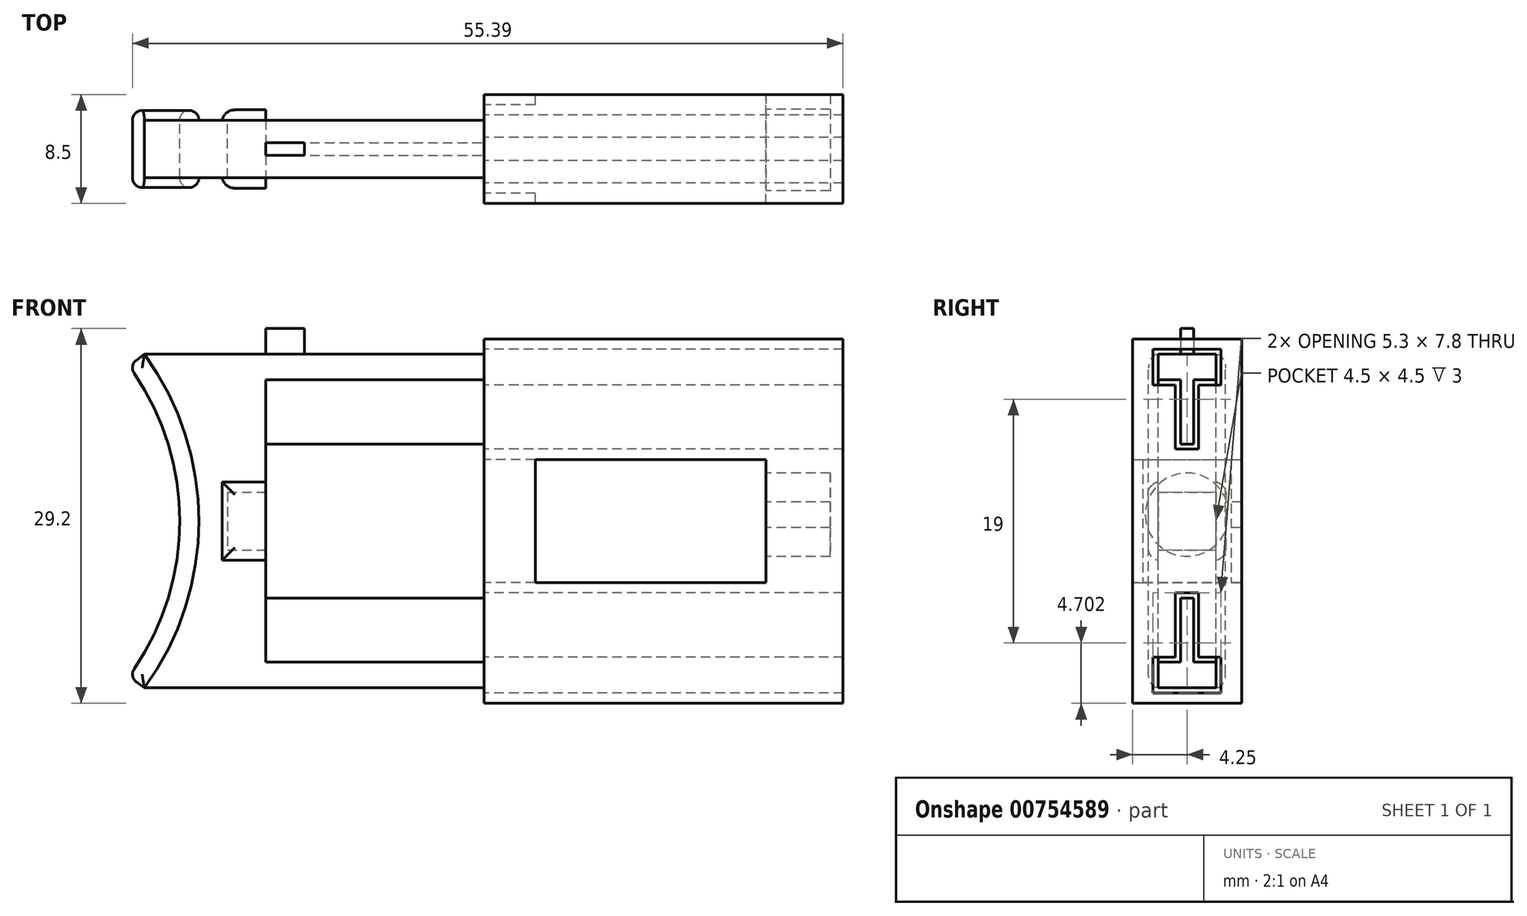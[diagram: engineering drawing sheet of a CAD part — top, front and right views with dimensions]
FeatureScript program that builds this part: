
annotation { "Feature Type Name" : "Feature", "Feature Type Description" : "" }
export const myFeature = defineFeature(function(context is Context, id is Id, definition is map)
    precondition{}
    {
        {
            var Q0;
            Q0=qCreatedBy(makeId("Front.planeOp"),FACE);
            var sketch = newSketch(context, id + "F0", { "sketchPlane" : qUnion([Q0])});
            skLineSegment(sketch, "E0.bottom", {"start": v(-9.54, 1.75) * mm, "end": v(-6.54, 1.75) * mm});
            skLineSegment(sketch, "E0.top", {"start": v(-9.54, -2.75) * mm, "end": v(-6.54, -2.75) * mm});
            skLineSegment(sketch, "E0.left", {"start": v(-9.54, 1.75) * mm, "end": v(-9.54, -2.75) * mm});
            skLineSegment(sketch, "E1.bottom", {"start": v(-16, 12.5) * mm, "end": v(-9.54, 12.5) * mm, "construction": true});
            skLineSegment(sketch, "E1.top", {"start": v(-16, -13.5) * mm, "end": v(-9.54, -13.5) * mm, "construction": true});
            skLineSegment(sketch, "E1.left", {"start": v(-9.54, 12.5) * mm, "end": v(-9.54, -13.5) * mm, "construction": true});
            skLineSegment(sketch, "E1.right", {"start": v(-16, 12.5) * mm, "end": v(-16, -13.5) * mm, "construction": true});
            skPoint(sketch, "E2", {"position": v(-9.54, -0.5) * mm});
            skArc(sketch, "E3", {"start": v(-16, -13.5) * mm, "mid": v(-11.75, -0.5) * mm, "end": v(-16, 12.5) * mm});
            skLineSegment(sketch, "E4", {"start": v(-16, -13.5) * mm, "end": v(10.46, -13.5) * mm});
            skPoint(sketch, "E4.endSnap0", {"position": v(-12.77, -13.5) * mm});
            skLineSegment(sketch, "E5", {"start": v(10.46, -13.5) * mm, "end": v(10.46, -5.75) * mm});
            skLineSegment(sketch, "E6", {"start": v(10.46, -5.75) * mm, "end": v(-6.54, -5.75) * mm});
            skLineSegment(sketch, "E7", {"start": v(-6.54, -5.75) * mm, "end": v(-6.54, -2.75) * mm});
            skLineSegment(sketch, "E8", {"start": v(-6.54, 1.75) * mm, "end": v(-6.54, 4.75) * mm});
            skLineSegment(sketch, "E9", {"start": v(-6.54, 4.75) * mm, "end": v(10.46, 4.75) * mm});
            skLineSegment(sketch, "E10", {"start": v(10.46, 4.75) * mm, "end": v(10.46, 12.5) * mm});
            skLineSegment(sketch, "E11", {"start": v(10.46, 12.5) * mm, "end": v(-16, 12.5) * mm});
            skSolve(sketch);
        }
        {
            var Q0;
            Q0=makeQuery(id+"F0.imprint","IMPRINT",FACE,{"disambiguationData":[TD([[makeQuery(id+"F0.imprint","IMPRINT",EDGE,{"derivedFrom":sQuery(id+"F0.wireOp",EDGE,"E0.bottom")}),1.0]])]});
            extrude(context, id + "F1", {"entities" : qUnion([Q0]), "endBound" : BoundingType.SYMMETRIC, "depth" : 4.5 * mm, "offsetDistance" : 25 * mm});
        }
        {
            var Q0;
            Q0=makeQuery(id+"F1.opExtrude","SWEPT_FACE",FACE,{"disambiguationData":[OSD([sQuery(id+"F0.wireOp",EDGE,"E8")])]});
            var sketch = newSketch(context, id + "F2", { "sketchPlane" : qUnion([Q0])});
            skLineSegment(sketch, "E12.0.0", {"start": v(2.25, -2.75) * mm, "end": v(2.25, 1.75) * mm});
            skLineSegment(sketch, "E12.0.1", {"start": v(2.25, 1.75) * mm, "end": v(-2.25, 1.75) * mm});
            skLineSegment(sketch, "E12.0.2", {"start": v(-2.25, 1.75) * mm, "end": v(-2.25, -2.75) * mm});
            skLineSegment(sketch, "E12.0.3", {"start": v(-2.25, -2.75) * mm, "end": v(2.25, -2.75) * mm});
            skLineSegment(sketch, "E13.0", {"start": v(3.05, -3.55) * mm, "end": v(3.05, 2.55) * mm});
            skLineSegment(sketch, "E13.1", {"start": v(-3.05, -3.55) * mm, "end": v(3.05, -3.55) * mm});
            skLineSegment(sketch, "E13.2", {"start": v(-3.05, 2.55) * mm, "end": v(-3.05, -3.55) * mm});
            skLineSegment(sketch, "E13.3", {"start": v(3.05, 2.55) * mm, "end": v(-3.05, 2.55) * mm});
            skSolve(sketch);
        }
        {
            var Q0;
            Q0 = qSketchRegion(id + "F2", true);
            extrude(context, id + "F3", {"entities" : qUnion([Q0]), "operationType" : NewBodyOperationType.ADD, "oppositeDirection" : true, "depth" : 3.4 * mm, "offsetDistance" : 25 * mm});
        }
        {
            var Q0;
            Q0=qCreatedBy(makeId("Front.planeOp"),FACE);
            var sketch = newSketch(context, id + "F4", { "sketchPlane" : qUnion([Q0])});
            skArc(sketch, "E14.0.0", {"start": v(-16, 12.5) * mm, "mid": v(-11.75, -0.5) * mm, "end": v(-16, -13.5) * mm});
            skArc(sketch, "E14.0.2", {"start": v(-16, -13.5) * mm, "mid": v(-11.75, -0.5) * mm, "end": v(-16, 12.5) * mm});
            skArc(sketch, "E15.0", {"start": v(-17.22, 11.62) * mm, "mid": v(-13.25, -0.5) * mm, "end": v(-17.22, -12.61) * mm});
            skLineSegment(sketch, "E16", {"start": v(-16, 12.5) * mm, "end": v(-17.22, 11.62) * mm});
            skLineSegment(sketch, "E17", {"start": v(-17.22, -12.61) * mm, "end": v(-16, -13.5) * mm});
            skSolve(sketch);
        }
        {
            var Q0;
            Q0 = qSketchRegion(id + "F4", true);
            extrude(context, id + "F5", {"entities" : qUnion([Q0]), "operationType" : NewBodyOperationType.ADD, "endBound" : BoundingType.SYMMETRIC, "depth" : 6 * mm, "offsetDistance" : 25 * mm});
        }
        {
            var Q0;
            Q0=makeQuery(id+"F5.opExtrude","CAP_FACE",FACE,{"disambiguationData":[OSD([sQuery(id+"F4.wireOp",EDGE,"E14.0.2"),sQuery(id+"F4.wireOp",EDGE,"E15.0"),sQuery(id+"F4.wireOp",EDGE,"E16"),sQuery(id+"F4.wireOp",EDGE,"E17")])],"isStart":false});
            var Q1;
            Q1=makeQuery(id+"F5.opExtrude","CAP_FACE",FACE,{"disambiguationData":[OSD([sQuery(id+"F4.wireOp",EDGE,"E14.0.2"),sQuery(id+"F4.wireOp",EDGE,"E15.0"),sQuery(id+"F4.wireOp",EDGE,"E16"),sQuery(id+"F4.wireOp",EDGE,"E17")])],"isStart":true});
            var Q2;
            Q2=makeQuery(id+"F5.opExtrude","SWEPT_EDGE",EDGE,{"disambiguationData":[OSD([sQuery(id+"F4.wireOp",EDGE,"E15.0"),sQuery(id+"F4.wireOp",EDGE,"E17")])]});
            var Q3;
            Q3=makeQuery(id+"F5.opExtrude","SWEPT_EDGE",EDGE,{"disambiguationData":[OSD([sQuery(id+"F4.wireOp",EDGE,"E15.0"),sQuery(id+"F4.wireOp",EDGE,"E16")])]});
            fillet(context, id + "F6", {"entities" : qUnion([Q0, Q1, Q2, Q3]), "radius" : (1.5 / 2) * mm, "tangentPropagation" : true, "allowEdgeOverflow" : false});
        }
        {
            var Q0;
            Q0=makeQuery(id+"F3.opExtrude","CAP_EDGE",EDGE,{"disambiguationData":[OSD([sQuery(id+"F2.wireOp",EDGE,"E13.2")])],"isStart":false});
            var Q1;
            Q1=makeQuery(id+"F3.opExtrude","CAP_EDGE",EDGE,{"disambiguationData":[OSD([sQuery(id+"F2.wireOp",EDGE,"E13.0")])],"isStart":false});
            var Q2;
            Q2=makeQuery(id+"F3.opExtrude","SWEPT_EDGE",EDGE,{"disambiguationData":[OSD([sQuery(id+"F2.wireOp",EDGE,"E13.1"),sQuery(id+"F2.wireOp",EDGE,"E13.2")])]});
            var Q3;
            Q3=makeQuery(id+"F3.opExtrude","SWEPT_EDGE",EDGE,{"disambiguationData":[OSD([sQuery(id+"F2.wireOp",EDGE,"E13.2"),sQuery(id+"F2.wireOp",EDGE,"E13.3")])]});
            var Q4;
            Q4=makeQuery(id+"F3.opExtrude","SWEPT_EDGE",EDGE,{"disambiguationData":[OSD([sQuery(id+"F2.wireOp",EDGE,"E13.0"),sQuery(id+"F2.wireOp",EDGE,"E13.3")])]});
            var Q5;
            Q5=makeQuery(id+"F3.opExtrude","SWEPT_EDGE",EDGE,{"disambiguationData":[OSD([sQuery(id+"F2.wireOp",EDGE,"E13.0"),sQuery(id+"F2.wireOp",EDGE,"E13.1")])]});
            fillet(context, id + "F7", {"entities" : qUnion([Q0, Q1, Q2, Q3, Q4, Q5]), "radius" : 1 * mm, "tangentPropagation" : true, "allowEdgeOverflow" : false});
        }
        {
            var Q0;
            Q0=makeQuery(id+"F1.opExtrude","SWEPT_FACE",FACE,{"disambiguationData":[OSD([sQuery(id+"F0.wireOp",EDGE,"E10")])]});
            var sketch = newSketch(context, id + "F8", { "sketchPlane" : qUnion([Q0])});
            skLineSegment(sketch, "E18.0", {"start": v(-2.25, 12.5) * mm, "end": v(2.25, 12.5) * mm});
            skLineSegment(sketch, "E19.0", {"start": v(-2.25, -13.5) * mm, "end": v(2.25, -13.5) * mm});
            skLineSegment(sketch, "E20", {"start": v(-2.25, 4.75) * mm, "end": v(2.25, 4.75) * mm});
            skLineSegment(sketch, "E21", {"start": v(2.25, 4.75) * mm, "end": v(2.25, 10.5) * mm});
            skLineSegment(sketch, "E22", {"start": v(2.25, 10.5) * mm, "end": v(0.5, 10.5) * mm});
            skLineSegment(sketch, "E23", {"start": v(0.5, 10.5) * mm, "end": v(0.5, 5.5) * mm});
            skLineSegment(sketch, "E24", {"start": v(0.5, 5.5) * mm, "end": v(-0.5, 5.5) * mm});
            skLineSegment(sketch, "E25", {"start": v(-0.5, 5.5) * mm, "end": v(-0.5, 10.5) * mm});
            skLineSegment(sketch, "E26", {"start": v(-0.5, 10.5) * mm, "end": v(-2.25, 10.5) * mm});
            skLineSegment(sketch, "E27", {"start": v(-2.25, 10.5) * mm, "end": v(-2.25, 4.75) * mm});
            skLineSegment(sketch, "E28", {"start": v(2.25, -5.75) * mm, "end": v(2.25, -11.5) * mm});
            skLineSegment(sketch, "E29", {"start": v(2.25, -11.5) * mm, "end": v(0.5, -11.5) * mm});
            skLineSegment(sketch, "E30", {"start": v(0.5, -11.5) * mm, "end": v(0.5, -6.5) * mm});
            skLineSegment(sketch, "E31", {"start": v(0.5, -6.5) * mm, "end": v(-0.5, -6.5) * mm});
            skLineSegment(sketch, "E32", {"start": v(-0.5, -6.5) * mm, "end": v(-0.5, -11.5) * mm});
            skLineSegment(sketch, "E33", {"start": v(-0.5, -11.5) * mm, "end": v(-2.25, -11.5) * mm});
            skLineSegment(sketch, "E34", {"start": v(-2.25, -11.5) * mm, "end": v(-2.25, -5.75) * mm});
            skLineSegment(sketch, "E35.0", {"start": v(-2.25, -5.75) * mm, "end": v(2.25, -5.75) * mm});
            skPoint(sketch, "E36", {"position": v(0, -6.5) * mm});
            skSolve(sketch);
        }
        {
            var Q0;
            Q0 = qSketchRegion(id + "F8", true);
            var Q1;
            Q1=makeQuery(id+"F3.boolean.opBoolean","MERGE",FACE,{"derivedFrom":[makeQuery(id+"F1.opExtrude","SWEPT_FACE",FACE,{"disambiguationData":[OSD([sQuery(id+"F0.wireOp",EDGE,"E7")])]}),makeQuery(id+"F1.opExtrude","SWEPT_FACE",FACE,{"disambiguationData":[OSD([sQuery(id+"F0.wireOp",EDGE,"E8")])]}),makeQuery(id+"F3.opExtrude","CAP_FACE",FACE,{"disambiguationData":[OSD([sQuery(id+"F2.wireOp",EDGE,"E12.0.0"),sQuery(id+"F2.wireOp",EDGE,"E12.0.1"),sQuery(id+"F2.wireOp",EDGE,"E12.0.2"),sQuery(id+"F2.wireOp",EDGE,"E12.0.3"),sQuery(id+"F2.wireOp",EDGE,"E13.0"),sQuery(id+"F2.wireOp",EDGE,"E13.1"),sQuery(id+"F2.wireOp",EDGE,"E13.2"),sQuery(id+"F2.wireOp",EDGE,"E13.3")])],"isStart":true})]});
            extrude(context, id + "F9", {"entities" : qUnion([Q0]), "operationType" : NewBodyOperationType.REMOVE, "endBound" : BoundingType.UP_TO_SURFACE, "oppositeDirection" : true, "depth" : 9.9 * mm, "endBoundEntityFace" : qUnion([Q1]), "offsetDistance" : 25 * mm});
        }
        {
            var Q0;
            Q0=makeQuery(id+"F1.opExtrude","SWEPT_FACE",FACE,{"disambiguationData":[OSD([sQuery(id+"F0.wireOp",EDGE,"E11")])]});
            var sketch = newSketch(context, id + "F10", { "sketchPlane" : qUnion([Q0])});
            skLineSegment(sketch, "E37.0.5", {"start": v(-6.54, 0.5) * mm, "end": v(-6.54, -0.5) * mm});
            skLineSegment(sketch, "E37.0.15", {"start": v(-6.54, -0.5) * mm, "end": v(-6.54, 0.5) * mm});
            skLineSegment(sketch, "E38.right", {"start": v(-3.54, -0.5) * mm, "end": v(-3.54, 0.5) * mm});
            skLineSegment(sketch, "E39", {"start": v(-6.54, -0.5) * mm, "end": v(-3.54, -0.5) * mm});
            skLineSegment(sketch, "E40", {"start": v(-6.54, 0.5) * mm, "end": v(-3.54, 0.5) * mm});
            skSolve(sketch);
        }
        {
            var Q0;
            Q0 = qSketchRegion(id + "F10", true);
            extrude(context, id + "F11", {"entities" : qUnion([Q0]), "operationType" : NewBodyOperationType.ADD, "depth" : 2 * mm, "offsetDistance" : 25 * mm});
        }
        {
            var Q0;
            Q0=makeQuery(id+"F1.opExtrude","SWEPT_FACE",FACE,{"disambiguationData":[OSD([sQuery(id+"F0.wireOp",EDGE,"E10")])]});
            var sketch = newSketch(context, id + "F12", { "sketchPlane" : qUnion([Q0])});
            skLineSegment(sketch, "E41.0.0", {"start": v(0.5, 10.5) * mm, "end": v(2.25, 10.5) * mm, "construction": true});
            skLineSegment(sketch, "E41.0.1", {"start": v(2.25, 10.5) * mm, "end": v(2.25, 12.5) * mm, "construction": true});
            skLineSegment(sketch, "E41.0.2", {"start": v(2.25, 12.5) * mm, "end": v(-2.25, 12.5) * mm, "construction": true});
            skLineSegment(sketch, "E41.0.3", {"start": v(-2.25, 12.5) * mm, "end": v(-2.25, 10.5) * mm, "construction": true});
            skLineSegment(sketch, "E41.0.4", {"start": v(-2.25, 10.5) * mm, "end": v(-0.5, 10.5) * mm, "construction": true});
            skLineSegment(sketch, "E41.0.5", {"start": v(-0.5, 10.5) * mm, "end": v(-0.5, 5.5) * mm, "construction": true});
            skLineSegment(sketch, "E41.0.6", {"start": v(-0.5, 5.5) * mm, "end": v(0.5, 5.5) * mm, "construction": true});
            skLineSegment(sketch, "E41.0.7", {"start": v(0.5, 5.5) * mm, "end": v(0.5, 10.5) * mm, "construction": true});
            skLineSegment(sketch, "E42.0.0", {"start": v(-0.5, -6.5) * mm, "end": v(-0.5, -11.5) * mm, "construction": true});
            skLineSegment(sketch, "E42.0.1", {"start": v(-0.5, -11.5) * mm, "end": v(-2.25, -11.5) * mm, "construction": true});
            skLineSegment(sketch, "E42.0.2", {"start": v(-2.25, -11.5) * mm, "end": v(-2.25, -13.5) * mm, "construction": true});
            skLineSegment(sketch, "E42.0.3", {"start": v(-2.25, -13.5) * mm, "end": v(2.25, -13.5) * mm, "construction": true});
            skLineSegment(sketch, "E42.0.4", {"start": v(2.25, -13.5) * mm, "end": v(2.25, -11.5) * mm, "construction": true});
            skLineSegment(sketch, "E42.0.5", {"start": v(2.25, -11.5) * mm, "end": v(0.5, -11.5) * mm, "construction": true});
            skLineSegment(sketch, "E42.0.6", {"start": v(0.5, -11.5) * mm, "end": v(0.5, -6.5) * mm, "construction": true});
            skLineSegment(sketch, "E42.0.7", {"start": v(0.5, -6.5) * mm, "end": v(-0.5, -6.5) * mm, "construction": true});
            skLineSegment(sketch, "E43.0.0", {"start": v(2.25, -2.75) * mm, "end": v(2.25, 1.75) * mm, "construction": true});
            skLineSegment(sketch, "E43.0.1", {"start": v(2.25, 1.75) * mm, "end": v(-2.25, 1.75) * mm, "construction": true});
            skLineSegment(sketch, "E43.0.2", {"start": v(-2.25, 1.75) * mm, "end": v(-2.25, -2.75) * mm, "construction": true});
            skLineSegment(sketch, "E43.0.3", {"start": v(-2.25, -2.75) * mm, "end": v(2.25, -2.75) * mm, "construction": true});
            skLineSegment(sketch, "E44.0", {"start": v(0.9, 5.1) * mm, "end": v(0.9, 10.1) * mm});
            skLineSegment(sketch, "E44.1", {"start": v(-0.9, 5.1) * mm, "end": v(0.9, 5.1) * mm});
            skLineSegment(sketch, "E44.2", {"start": v(0.9, 10.1) * mm, "end": v(2.65, 10.1) * mm});
            skLineSegment(sketch, "E44.3", {"start": v(-0.9, 10.1) * mm, "end": v(-0.9, 5.1) * mm});
            skLineSegment(sketch, "E44.4", {"start": v(2.65, 10.1) * mm, "end": v(2.65, 12.9) * mm});
            skLineSegment(sketch, "E44.5", {"start": v(2.65, 12.9) * mm, "end": v(-2.65, 12.9) * mm});
            skLineSegment(sketch, "E44.6", {"start": v(-2.65, 12.9) * mm, "end": v(-2.65, 10.1) * mm});
            skLineSegment(sketch, "E44.7", {"start": v(-2.65, 10.1) * mm, "end": v(-0.9, 10.1) * mm});
            skLineSegment(sketch, "E45.0", {"start": v(0.9, -6.1) * mm, "end": v(-0.9, -6.1) * mm});
            skLineSegment(sketch, "E45.1", {"start": v(0.9, -11.1) * mm, "end": v(0.9, -6.1) * mm});
            skLineSegment(sketch, "E45.2", {"start": v(-0.9, -6.1) * mm, "end": v(-0.9, -11.1) * mm});
            skLineSegment(sketch, "E45.3", {"start": v(2.65, -11.1) * mm, "end": v(0.9, -11.1) * mm});
            skLineSegment(sketch, "E45.4", {"start": v(-0.9, -11.1) * mm, "end": v(-2.65, -11.1) * mm});
            skLineSegment(sketch, "E45.5", {"start": v(-2.65, -11.1) * mm, "end": v(-2.65, -13.9) * mm});
            skLineSegment(sketch, "E45.6", {"start": v(-2.65, -13.9) * mm, "end": v(2.65, -13.9) * mm});
            skLineSegment(sketch, "E45.7", {"start": v(2.65, -13.9) * mm, "end": v(2.65, -11.1) * mm});
            skLineSegment(sketch, "E46.bottom", {"start": v(-4.25, 13.7) * mm, "end": v(4.25, 13.7) * mm});
            skLineSegment(sketch, "E46.top", {"start": v(-4.25, -14.7) * mm, "end": v(4.25, -14.7) * mm});
            skLineSegment(sketch, "E46.left", {"start": v(-4.25, 13.7) * mm, "end": v(-4.25, -14.7) * mm});
            skLineSegment(sketch, "E46.right", {"start": v(4.25, 13.7) * mm, "end": v(4.25, -14.7) * mm});
            skLineSegment(sketch, "E47.bottom", {"start": v(-3.45, 4.3) * mm, "end": v(3.45, 4.3) * mm});
            skLineSegment(sketch, "E47.top", {"start": v(-3.45, -5.3) * mm, "end": v(3.45, -5.3) * mm});
            skLineSegment(sketch, "E47.left", {"start": v(-3.45, 4.3) * mm, "end": v(-3.45, -5.3) * mm});
            skLineSegment(sketch, "E47.right", {"start": v(3.45, 4.3) * mm, "end": v(3.45, -5.3) * mm});
            skSolve(sketch);
        }
        {
            var Q0;
            Q0 = qSketchRegion(id + "F12", true);
            extrude(context, id + "F13", {"entities" : qUnion([Q0]), "depth" : 28 * mm, "offsetDistance" : 25 * mm});
        }
        {
            var Q0;
            Q0=makeQuery(id+"F13.opExtrude","CAP_FACE",FACE,{"disambiguationData":[OSD([sQuery(id+"F12.wireOp",EDGE,"E44.0"),sQuery(id+"F12.wireOp",EDGE,"E44.1"),sQuery(id+"F12.wireOp",EDGE,"E44.2"),sQuery(id+"F12.wireOp",EDGE,"E44.3"),sQuery(id+"F12.wireOp",EDGE,"E44.4"),sQuery(id+"F12.wireOp",EDGE,"E44.5"),sQuery(id+"F12.wireOp",EDGE,"E44.6"),sQuery(id+"F12.wireOp",EDGE,"E44.7"),sQuery(id+"F12.wireOp",EDGE,"E45.0"),sQuery(id+"F12.wireOp",EDGE,"E45.1"),sQuery(id+"F12.wireOp",EDGE,"E45.2"),sQuery(id+"F12.wireOp",EDGE,"E45.3"),sQuery(id+"F12.wireOp",EDGE,"E45.4"),sQuery(id+"F12.wireOp",EDGE,"E45.5"),sQuery(id+"F12.wireOp",EDGE,"E45.6"),sQuery(id+"F12.wireOp",EDGE,"E45.7"),sQuery(id+"F12.wireOp",EDGE,"E46.bottom"),sQuery(id+"F12.wireOp",EDGE,"E46.top"),sQuery(id+"F12.wireOp",EDGE,"E46.left"),sQuery(id+"F12.wireOp",EDGE,"E46.right"),sQuery(id+"F12.wireOp",EDGE,"E47.bottom"),sQuery(id+"F12.wireOp",EDGE,"E47.top"),sQuery(id+"F12.wireOp",EDGE,"E47.left"),sQuery(id+"F12.wireOp",EDGE,"E47.right")])],"isStart":false});
            var sketch = newSketch(context, id + "F14", { "sketchPlane" : qUnion([Q0])});
            skLineSegment(sketch, "E48.0", {"start": v(-3.45, 4.3) * mm, "end": v(3.45, 4.3) * mm});
            skPoint(sketch, "E49.0", {"position": v(0, -5.3) * mm});
            skLineSegment(sketch, "E50", {"start": v(3.45, -0.5) * mm, "end": v(-3.45, -0.5) * mm, "construction": true});
            skLineSegment(sketch, "E51", {"start": v(-3.45, -5.3) * mm, "end": v(3.45, -5.3) * mm});
            skLineSegment(sketch, "E52", {"start": v(-4.25, 4.3) * mm, "end": v(4.25, 4.3) * mm});
            skLineSegment(sketch, "E53", {"start": v(4.25, 4.3) * mm, "end": v(4.25, -5.3) * mm});
            skLineSegment(sketch, "E54", {"start": v(4.25, -5.3) * mm, "end": v(-4.25, -5.3) * mm});
            skLineSegment(sketch, "E55", {"start": v(-4.25, -5.3) * mm, "end": v(-4.25, 4.3) * mm});
            skSolve(sketch);
        }
        {
            var Q0;
            Q0=makeQuery(id+"F13.opExtrude","SWEPT_FACE",FACE,{"disambiguationData":[OSD([sQuery(id+"F12.wireOp",EDGE,"E46.right")])]});
            var sketch = newSketch(context, id + "F15", { "sketchPlane" : qUnion([Q0])});
            skLineSegment(sketch, "E56.0", {"start": v(-10.46, 4.3) * mm, "end": v(-10.46, -5.3) * mm});
            skLineSegment(sketch, "E57.bottom", {"start": v(-36.46, 4.3) * mm, "end": v(-14.46, 4.3) * mm});
            skLineSegment(sketch, "E57.top", {"start": v(-36.46, -5.3) * mm, "end": v(-14.46, -5.3) * mm});
            skLineSegment(sketch, "E57.left", {"start": v(-36.46, 4.3) * mm, "end": v(-36.46, -5.3) * mm});
            skLineSegment(sketch, "E57.right", {"start": v(-14.46, 4.3) * mm, "end": v(-14.46, -5.3) * mm});
            skLineSegment(sketch, "E58.0", {"start": v(-38.46, 4.3) * mm, "end": v(-38.46, -5.3) * mm});
            skSolve(sketch);
        }
        {
            var Q0;
            Q0 = qSketchRegion(id + "F15", true);
            extrude(context, id + "F16", {"entities" : qUnion([Q0]), "operationType" : NewBodyOperationType.REMOVE, "oppositeDirection" : true, "depth" : 15.5 * mm, "offsetDistance" : 25 * mm});
        }
        {
            var Q0;
            Q0 = qSketchRegion(id + "F14", true);
            extrude(context, id + "F17", {"entities" : qUnion([Q0]), "operationType" : NewBodyOperationType.ADD, "oppositeDirection" : true, "depth" : (1 + 5) * mm, "offsetDistance" : 25 * mm});
        }
        {
            var Q0;
            Q0=makeQuery(id+"F17.opExtrude","CAP_FACE",FACE,{"disambiguationData":[OSD([sQuery(id+"F14.wireOp",EDGE,"E52"),sQuery(id+"F14.wireOp",EDGE,"E53"),sQuery(id+"F14.wireOp",EDGE,"E54"),sQuery(id+"F14.wireOp",EDGE,"E55")])],"isStart":false});
            var sketch = newSketch(context, id + "F18", { "sketchPlane" : qUnion([Q0])});
            skLineSegment(sketch, "E59.0.0", {"start": v(-4.25, -5.3) * mm, "end": v(4.25, -5.3) * mm, "construction": true});
            skLineSegment(sketch, "E59.0.1", {"start": v(4.25, -5.3) * mm, "end": v(4.25, 4.3) * mm, "construction": true});
            skLineSegment(sketch, "E59.0.2", {"start": v(4.25, 4.3) * mm, "end": v(-4.25, 4.3) * mm, "construction": true});
            skLineSegment(sketch, "E59.0.3", {"start": v(-4.25, 4.3) * mm, "end": v(-4.25, -5.3) * mm, "construction": true});
            skLineSegment(sketch, "E60", {"start": v(4.25, 0) * mm, "end": v(-4.25, 0) * mm, "construction": true});
            skCircle(sketch, "E61", {"center": v(0, 0) * mm, "radius": 3.25 * mm});
            skLineSegment(sketch, "E62.bottom", {"start": v(-4.25, 1) * mm, "end": v(-3.1, 1) * mm});
            skLineSegment(sketch, "E62.top", {"start": v(-4.25, -1) * mm, "end": v(-3.1, -1) * mm});
            skLineSegment(sketch, "E62.left", {"start": v(-4.25, 1) * mm, "end": v(-4.25, -1) * mm});
            skPoint(sketch, "E63.orphan", {"position": v(0, 1) * mm});
            skPoint(sketch, "E64.orphan", {"position": v(0, -1) * mm});
            skSolve(sketch);
        }
        {
            var Q0;
            Q0 = qSketchRegion(id + "F18", true);
            extrude(context, id + "F19", {"entities" : qUnion([Q0]), "operationType" : NewBodyOperationType.REMOVE, "oppositeDirection" : true, "depth" : 5 * mm, "offsetDistance" : 25 * mm});
        }
    });
